# Revit family: Sink_Floor_Industrial_12x12x6_Zurn-Z1850
name_source: partatom
category: Plumbing Fixtures
units: mm (PartAtom-declared; Revit-internal decimal feet)

## family parameters
Always vertical = Yes
Cut with Voids When Loaded = No
Maintain Annotation Orientation = No
OmniClass Number = 23.70.50.21.24.14
OmniClass Title = Deck Waste Water Drains
Part Type = Normal
Room Calculation Point = No
Round Connector Dimension = Use Radius
Shared = No
Work Plane-Based = No

## types (32) — shared parameters
Approx. Weight (Lbs) = 10 "
Assembly Code = D2030300
CW Connection = No
Default Elevation = 2 "
Description = 12” x 12” [305 x 305] SQUARE x 6” [152] DEEP INDUSTRIAL SANITARY FLOOR SINK
HW Connection = No
Manufacturer = Zurn Water, LLC
Manufacurer Brand = Zurn
Modified Date = 10/14/25
Product Documentation Link = https://files.zurn.com
Product Page URL = https://www.zurn.com
Product data url = https://www.bimobject.com
Sump Height = 6 "
URL = www.zurn.com
Vent Connection = No
WFU = 1
Waste Connection = Yes
zero-valued in all types: CWFU, HWFU

## per-type parameters (varying)
| type | 'E' Outlet HT Dim | Main Material | Model | Pipe Size 'A' (Inner Diameter) | Pipe Size 'A' (Inner Radius) | Pipe Size 'A' (Nominal Diameter) | Pipe Size 'A' (Nominal Radius) | Pipe Size 'A' (Outer Diameter) | Pipe Size 'A' (Outer Radius) | Type Comments |
| Z1850-2BW | 9 " | Steel - Zurn - Stainless - Type - 304 | Z1850 | 2.067 " | 1.034 " | 2 " | 1 " | 2.375 " | 1.188 " | Z1850 2 inch Butt-Weld Outlet |
| Z1850-3BW | 9 " | Steel - Zurn - Stainless - Type - 304 | Z1850 | 3.068 " | 1.534 " | 3 " | 1.5 " | 3.5 " | 1.75 " | Z1850 3 inch Butt-Weld Outlet |
| Z1850-4BW | 9 " | Steel - Zurn - Stainless - Type - 304 | Z1850 | 4.026 " | 2.013 " | 4 " | 2 " | 4.5 " | 2.25 " | Z1850 4 inch Butt-Weld Outlet |
| Z1850-6BW | 9 " | Steel - Zurn - Stainless - Type - 304 | Z1850 | 6.065 " | 3.033 " | 6 " | 3 " | 6.625 " | 3.313 " | Z1850 6 inch Butt-Weld Outlet |
| Z1850-2NH | 9 " | Steel - Zurn - Stainless - Type - 304 | Z1850 | 2.067 " | 1.034 " | 2 " | 1 " | 2.375 " | 1.188 " | Z1850 2 inch No-Hub Outlet |
| Z1850-3NH | 9 " | Steel - Zurn - Stainless - Type - 304 | Z1850 | 3.068 " | 1.534 " | 3 " | 1.5 " | 3.5 " | 1.75 " | Z1850 3 inch No-Hub Outlet |
| Z1850-4NH | 9 " | Steel - Zurn - Stainless - Type - 304 | Z1850 | 4.026 " | 2.013 " | 4 " | 2 " | 4.5 " | 2.25 " | Z1850 4 inch No-Hub Outlet |
| Z1850-6NH | 9 " | Steel - Zurn - Stainless - Type - 304 | Z1850 | 6.065 " | 3.033 " | 6 " | 3 " | 6.625 " | 3.313 " | Z1850 6 inch No-Hub Outlet |
| Z1850-2IP | 9 " | Steel - Zurn - Stainless - Type - 304 | Z1850 | 2.067 " | 1.034 " | 2 " | 1 " | 2.375 " | 1.188 " | Z1850 2 inch Threaded Outlet |
| Z1850-3IP | 9 " | Steel - Zurn - Stainless - Type - 304 | Z1850 | 3.068 " | 1.534 " | 3 " | 1.5 " | 3.5 " | 1.75 " | Z1850 3 inch Threaded Outlet |
| Z1850-4IP | 9 " | Steel - Zurn - Stainless - Type - 304 | Z1850 | 4.026 " | 2.013 " | 4 " | 2 " | 4.5 " | 2.25 " | Z1850 4 inch Threaded Outlet |
| Z1850-6IP | 9 " | Steel - Zurn - Stainless - Type - 304 | Z1850 | 6.065 " | 3.033 " | 6 " | 3 " | 6.625 " | 3.313 " | Z1850 6 inch Threaded Outlet |
| Z1850-2A | 7.25 " | Steel - Zurn - Stainless - Type - 304 | Z1850 | 2.067 " | 1.034 " | 2 " | 1 " | 2.375 " | 1.188 " | Z1850 2 inch Adjustable Threaded Outlet |
| Z1850-3A | 7.5 " | Steel - Zurn - Stainless - Type - 304 | Z1850 | 3.068 " | 1.534 " | 3 " | 1.5 " | 3.5 " | 1.75 " | Z1850 3 inch Adjustable Threaded Outlet |
| Z1850-4A | 7.5 " | Steel - Zurn - Stainless - Type - 304 | Z1850 | 4.026 " | 2.013 " | 4 " | 2 " | 4.5 " | 2.25 " | Z1850 4 inch Adjustable Threaded Outlet |
| Z1850-6A | 8.5 " | Steel - Zurn - Stainless - Type - 304 | Z1850 | 6.065 " | 3.033 " | 6 " | 3 " | 6.625 " | 3.313 " | Z1850 6 inch Adjustable Threaded Outlet |
| ZM1850-2BW | 9 " | Steel - Zurn - Stainless - Type - 316 | ZM1850 | 2.067 " | 1.034 " | 2 " | 1 " | 2.375 " | 1.188 " | ZM1850 2 inch Butt-Weld Outlet |
| ZM1850-3BW | 9 " | Steel - Zurn - Stainless - Type - 316 | ZM1850 | 3.068 " | 1.534 " | 3 " | 1.5 " | 3.5 " | 1.75 " | ZM1850 3 inch Butt-Weld Outlet |
| ZM1850-4BW | 9 " | Steel - Zurn - Stainless - Type - 316 | ZM1850 | 4.026 " | 2.013 " | 4 " | 2 " | 4.5 " | 2.25 " | ZM1850 4 inch Butt-Weld Outlet |
| ZM1850-6BW | 9 " | Steel - Zurn - Stainless - Type - 316 | ZM1850 | 6.065 " | 3.033 " | 6 " | 3 " | 6.625 " | 3.313 " | ZM1850 6 inch Butt-Weld Outlet |
| ZM1850-2NH | 9 " | Steel - Zurn - Stainless - Type - 316 | ZM1850 | 2.067 " | 1.034 " | 2 " | 1 " | 2.375 " | 1.188 " | ZM1850 2 inch No-Hub Outlet |
| ZM1850-3NH | 9 " | Steel - Zurn - Stainless - Type - 316 | ZM1850 | 3.068 " | 1.534 " | 3 " | 1.5 " | 3.5 " | 1.75 " | ZM1850 3 inch No-Hub Outlet |
| ZM1850-4NH | 9 " | Steel - Zurn - Stainless - Type - 316 | ZM1850 | 4.026 " | 2.013 " | 4 " | 2 " | 4.5 " | 2.25 " | ZM1850 4 inch No-Hub Outlet |
| ZM1850-6NH | 9 " | Steel - Zurn - Stainless - Type - 316 | ZM1850 | 6.065 " | 3.033 " | 6 " | 3 " | 6.625 " | 3.313 " | ZM1850 6 inch No-Hub Outlet |
| ZM1850-2IP | 9 " | Steel - Zurn - Stainless - Type - 316 | ZM1850 | 2.067 " | 1.034 " | 2 " | 1 " | 2.375 " | 1.188 " | ZM1850 2 inch Threaded Outlet |
| ZM1850-3IP | 9 " | Steel - Zurn - Stainless - Type - 316 | ZM1850 | 3.068 " | 1.534 " | 3 " | 1.5 " | 3.5 " | 1.75 " | ZM1850 3 inch Threaded Outlet |
| ZM1850-4IP | 9 " | Steel - Zurn - Stainless - Type - 316 | ZM1850 | 4.026 " | 2.013 " | 4 " | 2 " | 4.5 " | 2.25 " | ZM1850 4 inch Threaded Outlet |
| ZM1850-6IP | 9 " | Steel - Zurn - Stainless - Type - 316 | ZM1850 | 6.065 " | 3.033 " | 6 " | 3 " | 6.625 " | 3.313 " | ZM1850 6 inch Threaded Outlet |
| ZM1850-2A | 7.25 " | Steel - Zurn - Stainless - Type - 316 | ZM1850 | 2.067 " | 1.034 " | 2 " | 1 " | 2.375 " | 1.188 " | ZM1850 2 inch Adjustable Threaded Outlet |
| ZM1850-3A | 7.5 " | Steel - Zurn - Stainless - Type - 316 | ZM1850 | 3.068 " | 1.534 " | 3 " | 1.5 " | 3.5 " | 1.75 " | ZM1850 3 inch Adjustable Threaded Outlet |
| ZM1850-4A | 7.5 " | Steel - Zurn - Stainless - Type - 316 | ZM1850 | 4.026 " | 2.013 " | 4 " | 2 " | 4.5 " | 2.25 " | ZM1850 4 inch Adjustable Threaded Outlet |
| ZM1850-6A | 8.5 " | Steel - Zurn - Stainless - Type - 316 | ZM1850 | 6.065 " | 3.033 " | 6 " | 3 " | 6.625 " | 3.313 " | ZM1850 6 inch Adjustable Threaded Outlet |

## geometry (parser evidence)
native form markers: Sweep x5
no freeform markers — native parametric forms only
